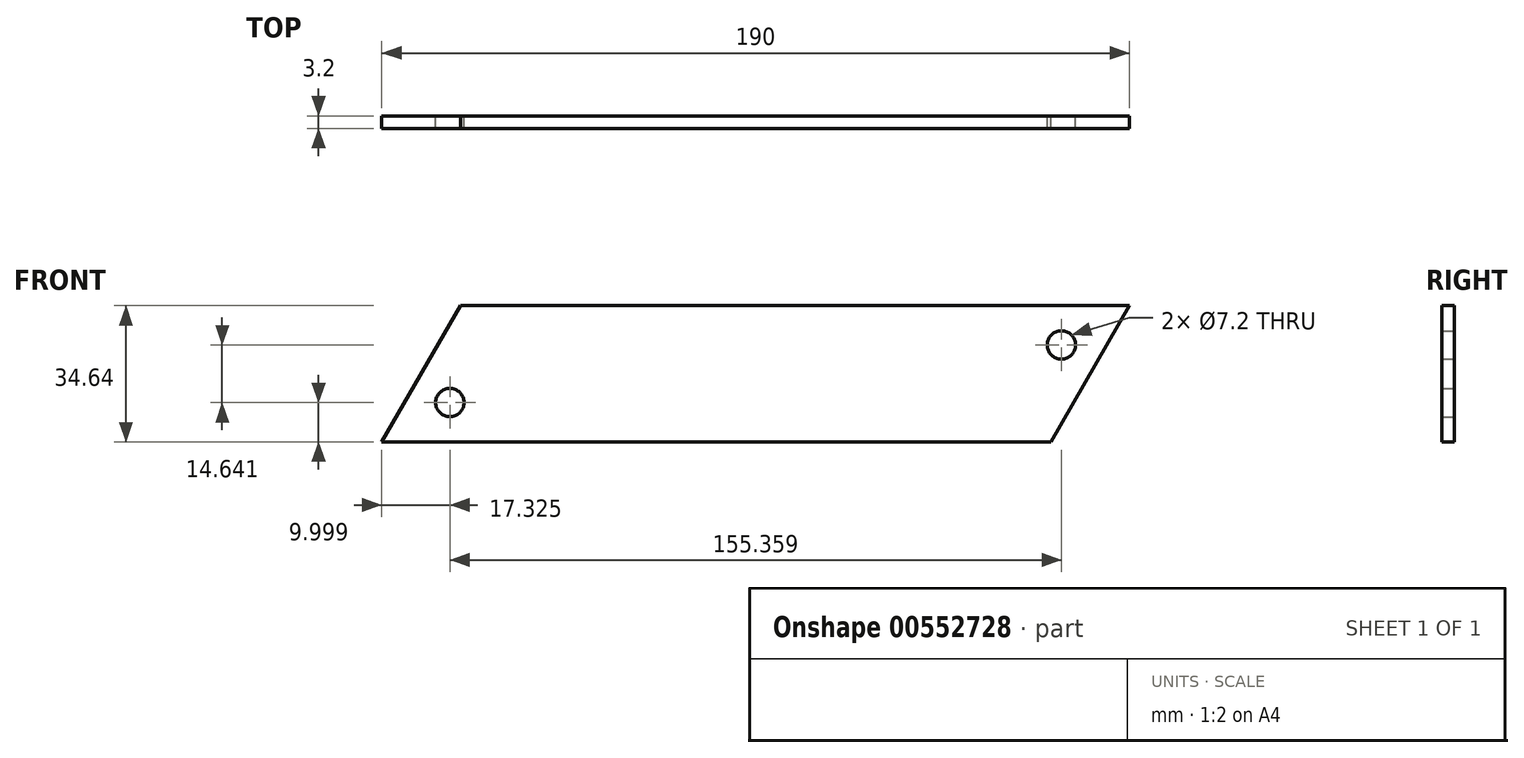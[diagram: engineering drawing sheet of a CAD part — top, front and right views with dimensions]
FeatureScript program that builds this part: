
annotation { "Feature Type Name" : "Feature", "Feature Type Description" : "" }
export const myFeature = defineFeature(function(context is Context, id is Id, definition is map)
    precondition{}
    {
        {
            var Q0;
            Q0=qCreatedBy(makeId("Front.planeOp"),FACE);
            var sketch = newSketch(context, id + "F0", { "sketchPlane" : qUnion([Q0])});
            skLineSegment(sketch, "E0.bottom", {"start": v(103.12, 13) * mm, "end": v(-66.88, 13) * mm});
            skPoint(sketch, "E0.middle", {"position": v(-66.88, 13) * mm});
            skLineSegment(sketch, "E1", {"start": v(103.13, 13) * mm, "end": v(83.12, -21.65) * mm});
            skLineSegment(sketch, "E2", {"start": v(-66.88, 13) * mm, "end": v(-86.88, -21.65) * mm});
            skLineSegment(sketch, "E3", {"start": v(-86.88, -21.65) * mm, "end": v(83.12, -21.65) * mm});
            skLineSegment(sketch, "E4", {"start": v(-66.88, 13) * mm, "end": v(103.12, 13) * mm});
            skCircle(sketch, "E5", {"center": v(-69.55, -11.65) * mm, "radius": 3.6 * mm});
            skCircle(sketch, "E6.MirrorC", {"center": v(85.8, 3) * mm, "radius": 3.6 * mm});
            skSolve(sketch);
        }
        {
            var Q0;
            Q0=qSketchRegion(id+"F0",true);
            extrude(context, id + "F1", {"entities" : qUnion([Q0]), "depth" : 3.2 * mm, "offsetDistance" : 25 * mm});
        }
    });
